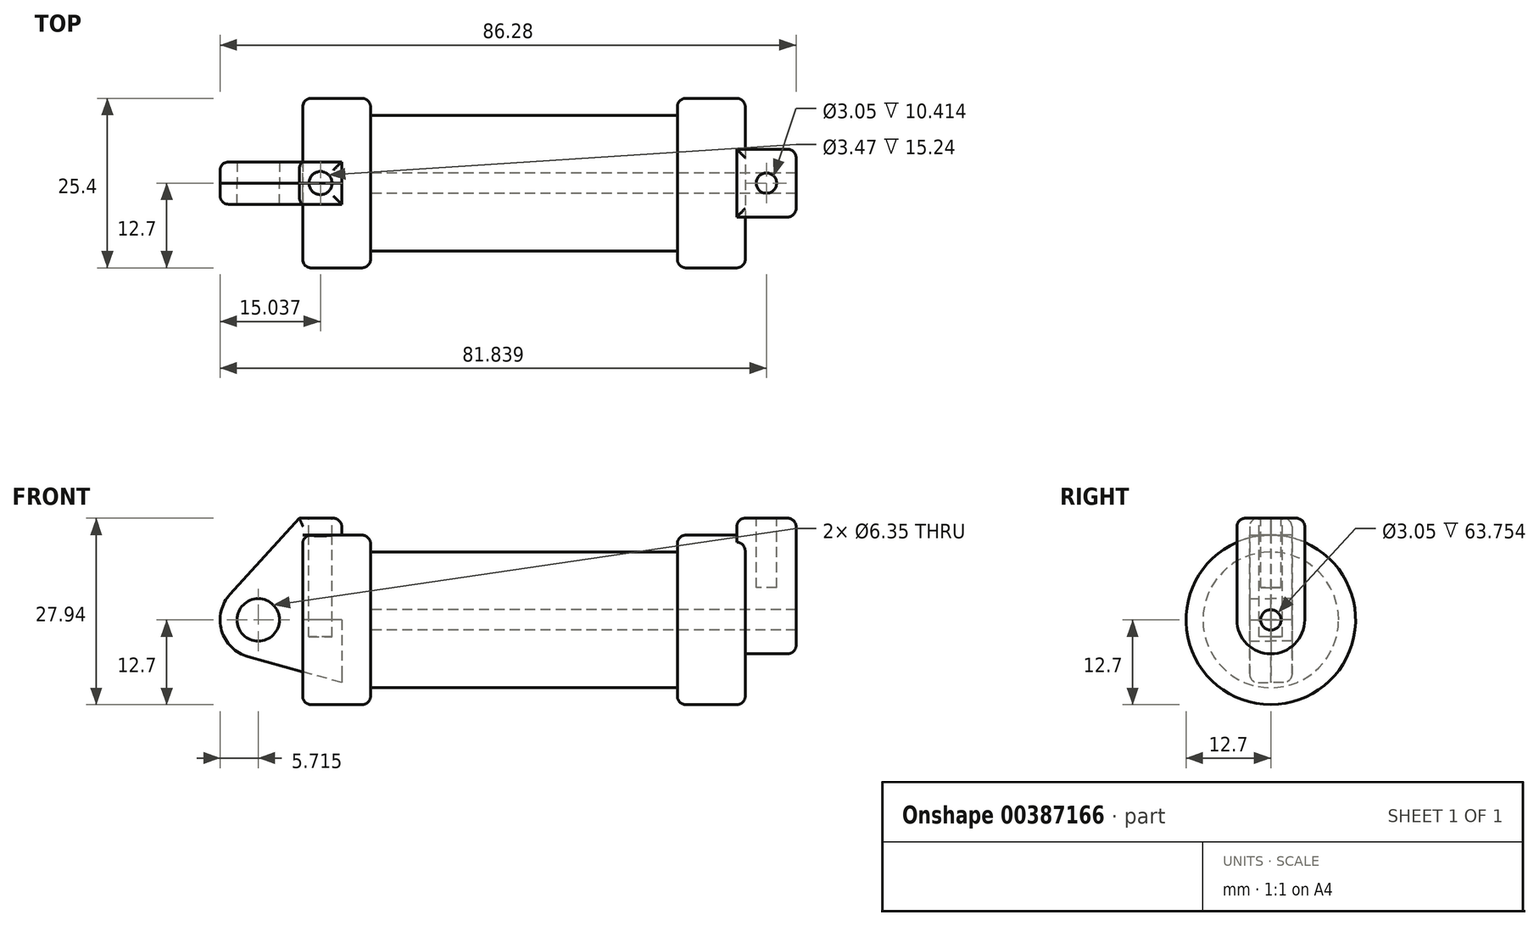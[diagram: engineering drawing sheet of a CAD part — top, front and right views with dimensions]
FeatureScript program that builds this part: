
annotation { "Feature Type Name" : "Feature", "Feature Type Description" : "" }
export const myFeature = defineFeature(function(context is Context, id is Id, definition is map)
    precondition{}
    {
        {
            var Q0;
            Q0=qCreatedBy(makeId("Front.planeOp"),FACE);
            var sketch = newSketch(context, id + "F0", { "sketchPlane" : qUnion([Q0])});
            skLineSegment(sketch, "E0", {"start": v(0, 0) * mm, "end": v(0, 12.7) * mm});
            skLineSegment(sketch, "E1", {"start": v(0, 12.7) * mm, "end": v(10.16, 12.7) * mm});
            skLineSegment(sketch, "E2", {"start": v(10.16, 12.7) * mm, "end": v(10.16, 10.16) * mm});
            skLineSegment(sketch, "E3", {"start": v(10.16, 10.16) * mm, "end": v(56.13, 10.16) * mm});
            skLineSegment(sketch, "E4", {"start": v(56.13, 10.16) * mm, "end": v(56.13, 12.7) * mm});
            skLineSegment(sketch, "E5", {"start": v(56.13, 12.7) * mm, "end": v(66.3, 12.7) * mm});
            skLineSegment(sketch, "E6", {"start": v(66.3, 12.7) * mm, "end": v(66.3, 0) * mm});
            skLineSegment(sketch, "E7", {"start": v(66.3, 0) * mm, "end": v(0, 0) * mm});
            skLineSegment(sketch, "E8", {"start": v(5.84, 15.24) * mm, "end": v(-0.5, 15.24) * mm});
            skLineSegment(sketch, "E9", {"start": v(-0.5, 15.24) * mm, "end": v(-10.88, 3.85) * mm});
            skLineSegment(sketch, "E10", {"start": v(0, 0) * mm, "end": v(-6.65, 0) * mm});
            skCircle(sketch, "E11", {"center": v(-6.65, 0) * mm, "radius": 5.72 * mm});
            skCircle(sketch, "E12", {"center": v(-6.65, 0) * mm, "radius": 3.18 * mm});
            skLineSegment(sketch, "E13", {"start": v(5.84, 15.24) * mm, "end": v(5.84, -9.4) * mm});
            skLineSegment(sketch, "E14", {"start": v(5.84, -9.4) * mm, "end": v(-8.18, -5.5) * mm});
            skSolve(sketch);
        }
        {
            var Q0;
            {var subQ0=sQuery(id+"F0.wireOp",EDGE,"E0");Q0=makeQuery(id+"F0.imprint","IMPRINT",FACE,{"disambiguationData":[TD([[makeQuery(id+"F0.imprint","IMPRINT",EDGE,{"derivedFrom":subQ0}),-1.0]])]});}
            var Q1;
            Q1=sQuery(id+"F0.wireOp",EDGE,"E7");
            revolve(context, id + "F1", {"entities" : qUnion([Q0]), "axis" : qUnion([Q1]), "revolveType" : RevolveType.FULL});
        }
        {
            var Q0;
            {var subQ0=sQuery(id+"F0.wireOp",EDGE,"E2");Q0=makeQuery(id+"F0.imprint","IMPRINT",FACE,{"disambiguationData":[TD([[makeQuery(id+"F0.imprint","IMPRINT",EDGE,{"derivedFrom":subQ0}),-1.0]])]});}
            var Q1;
            Q1=sQuery(id+"F0.wireOp",EDGE,"E7");
            revolve(context, id + "F2", {"operationType" : NewBodyOperationType.ADD, "entities" : qUnion([Q0]), "axis" : qUnion([Q1]), "revolveType" : RevolveType.FULL});
        }
        {
            var Q0;
            {var subQ5=sQuery(id+"F0.wireOp",EDGE,"E12");Q0=makeQuery(id+"F0.imprint","IMPRINT",FACE,{"disambiguationData":[TD([[makeQuery(id+"F0.imprint","IMPRINT",EDGE,{"derivedFrom":subQ5}),-1.0]])]});}
            var Q1;
            {var subQ0=sQuery(id+"F0.wireOp",EDGE,"E14");Q1=makeQuery(id+"F0.imprint","IMPRINT",FACE,{"disambiguationData":[TD([[makeQuery(id+"F0.imprint","IMPRINT",EDGE,{"derivedFrom":subQ0}),-1.0]])]});}
            var Q2;
            {var subQ1=sQuery(id+"F0.wireOp",EDGE,"E0");Q2=makeQuery(id+"F0.imprint","IMPRINT",FACE,{"disambiguationData":[TD([[makeQuery(id+"F0.imprint","IMPRINT",EDGE,{"derivedFrom":subQ1}),1.0]])]});}
            extrude(context, id + "F3", {"entities" : qUnion([Q0, Q1, Q2]), "depth" : 3.17 * mm});
        }
        {
            var Q0;
            {var subQ1=sQuery(id+"F0.wireOp",EDGE,"E0");Q0=makeQuery(id+"F0.imprint","IMPRINT",FACE,{"disambiguationData":[TD([[makeQuery(id+"F0.imprint","IMPRINT",EDGE,{"derivedFrom":subQ1}),1.0]])]});}
            var Q1;
            {var subQ5=sQuery(id+"F0.wireOp",EDGE,"E12");Q1=makeQuery(id+"F0.imprint","IMPRINT",FACE,{"disambiguationData":[TD([[makeQuery(id+"F0.imprint","IMPRINT",EDGE,{"derivedFrom":subQ5}),-1.0]])]});}
            var Q2;
            {var subQ0=sQuery(id+"F0.wireOp",EDGE,"E14");Q2=makeQuery(id+"F0.imprint","IMPRINT",FACE,{"disambiguationData":[TD([[makeQuery(id+"F0.imprint","IMPRINT",EDGE,{"derivedFrom":subQ0}),-1.0]])]});}
            extrude(context, id + "F4", {"entities" : qUnion([Q0, Q1, Q2]), "oppositeDirection" : true, "depth" : 3.17 * mm});
        }
        {
            var Q0;
            Q0=makeQuery(id+"F2.opRevolve","SWEPT_FACE",FACE,{"disambiguationData":[OSD([sQuery(id+"F0.wireOp",EDGE,"E6")])]});
            var sketch = newSketch(context, id + "F5", { "sketchPlane" : qUnion([Q0])});
            skCircle(sketch, "E15", {"center": v(0, 0) * mm, "radius": 1.52 * mm});
            skCircle(sketch, "E16", {"center": v(0, 0) * mm, "radius": 5.08 * mm});
            skLineSegment(sketch, "E17", {"start": v(-5.08, 0) * mm, "end": v(-5.08, 15.24) * mm});
            skLineSegment(sketch, "E18", {"start": v(5.08, 0) * mm, "end": v(5.08, 15.24) * mm});
            skLineSegment(sketch, "E19", {"start": v(-5.08, 15.24) * mm, "end": v(-3.2, 15.24) * mm});
            skLineSegment(sketch, "E20", {"start": v(-3.2, 15.24) * mm, "end": v(5.08, 15.24) * mm});
            skSolve(sketch);
        }
        {
            var Q0;
            Q0 = qSketchRegion(id + "F5", true);
            extrude(context, id + "F6", {"entities" : qUnion([Q0]), "operationType" : NewBodyOperationType.ADD, "depth" : 7.62 * mm});
        }
        {
            var Q0;
            Q0 = qSketchRegion(id + "F5", true);
            var Q1;
            Q1=makeQuery(id+"F5.imprint","IMPRINT",FACE,{"disambiguationData":[TD([[makeQuery(id+"F5.imprint","IMPRINT",EDGE,{"derivedFrom":sQuery(id+"F5.wireOp",EDGE,"E15")}),1.0]])]});
            extrude(context, id + "F7", {"entities" : qUnion([Q0, Q1]), "operationType" : NewBodyOperationType.ADD, "oppositeDirection" : true, "depth" : 1.27 * mm});
        }
        {
            var Q0;
            Q0=makeQuery(id+"F6.boolean.opBoolean","SPLIT",FACE,{"disambiguationData":[TD([makeQuery(id+"F6.opExtrude","SWEPT_FACE",FACE,{"disambiguationData":[OSD([sQuery(id+"F5.wireOp",EDGE,"E15")])]})])],"derivedFrom":makeQuery(id+"F2.opRevolve","SWEPT_FACE",FACE,{"disambiguationData":[OSD([sQuery(id+"F0.wireOp",EDGE,"E6")])]})});
            var Q1;
            Q1=makeQuery(id+"F2.opRevolve","SWEPT_FACE",FACE,{"disambiguationData":[OSD([sQuery(id+"F0.wireOp",EDGE,"E2")])]});
            extrude(context, id + "F8", {"entities" : qUnion([Q0]), "operationType" : NewBodyOperationType.REMOVE, "endBound" : BoundingType.UP_TO_SURFACE, "oppositeDirection" : true, "endBoundEntityFace" : qUnion([Q1]), "depth" : 25.4 * mm});
        }
        {
            var Q0;
            {var subQ0=sQuery(id+"F5.wireOp",EDGE,"E20");var subQ1=sQuery(id+"F5.wireOp",EDGE,"E19");Q0=makeQuery(id+"F7.boolean.opBoolean","MERGE",FACE,{"derivedFrom":[makeQuery(id+"F6.opExtrude","SWEPT_FACE",FACE,{"disambiguationData":[OSD([subQ1,subQ0])]}),makeQuery(id+"F7.opExtrude","SWEPT_FACE",FACE,{"disambiguationData":[OSD([subQ1,subQ0])]})]});}
            var sketch = newSketch(context, id + "F9", { "sketchPlane" : qUnion([Q0])});
            skLineSegment(sketch, "E21", {"start": v(69.47, 5.08) * mm, "end": v(69.47, -5.08) * mm, "construction": true});
            skLineSegment(sketch, "E22", {"start": v(73.91, 0) * mm, "end": v(65.02, 0) * mm, "construction": true});
            skCircle(sketch, "E23", {"center": v(69.47, 0) * mm, "radius": 1.52 * mm});
            skSolve(sketch);
        }
        {
            var Q0;
            Q0=makeQuery(id+"F9.imprint","IMPRINT",FACE,{"disambiguationData":[TD([[makeQuery(id+"F9.imprint","IMPRINT",EDGE,{"derivedFrom":sQuery(id+"F9.wireOp",EDGE,"E23")}),1.0]])]});
            extrude(context, id + "F10", {"entities" : qUnion([Q0]), "operationType" : NewBodyOperationType.REMOVE, "oppositeDirection" : true, "depth" : 10.4 * mm});
        }
        {
            var Q0;
            Q0=makeQuery(id+"F4.opExtrude","SWEPT_FACE",FACE,{"disambiguationData":[OSD([sQuery(id+"F0.wireOp",EDGE,"E8")])]});
            var sketch = newSketch(context, id + "F11", { "sketchPlane" : qUnion([Q0])});
            skCircle(sketch, "E24", {"center": v(2.67, 0) * mm, "radius": 1.73 * mm});
            skSolve(sketch);
        }
        {
            var Q0;
            {var subQ0=sQuery(id+"F11.wireOp",EDGE,"E24");var subQ1=makeQuery(id+"F4.opExtrude","CAP_EDGE",EDGE,{"disambiguationData":[OSD([sQuery(id+"F0.wireOp",EDGE,"E8")])],"isStart":true});var subQ2=makeQuery(id+"F11.imprint","INTERSECT",VERTEX,{"disambiguationData":[OD(0.0)],"derivedFrom":[subQ1,subQ0]});Q0=makeQuery(id+"F11.imprint","IMPRINT",FACE,{"disambiguationData":[TD([[makeQuery(id+"F11.imprint","IMPRINT",EDGE,{"disambiguationData":[TD([[subQ2,-1.0]])],"derivedFrom":subQ0}),1.0]])]});}
            var Q1;
            {var subQ0=sQuery(id+"F11.wireOp",EDGE,"E24");var subQ1=makeQuery(id+"F4.opExtrude","CAP_EDGE",EDGE,{"disambiguationData":[OSD([sQuery(id+"F0.wireOp",EDGE,"E8")])],"isStart":true});var subQ2=makeQuery(id+"F11.imprint","INTERSECT",VERTEX,{"disambiguationData":[OD(0.0)],"derivedFrom":[subQ1,subQ0]});Q1=makeQuery(id+"F11.imprint","IMPRINT",FACE,{"disambiguationData":[TD([[makeQuery(id+"F11.imprint","IMPRINT",EDGE,{"disambiguationData":[TD([[subQ2,1.0]])],"derivedFrom":subQ0}),1.0]])]});}
            extrude(context, id + "F12", {"entities" : qUnion([Q0, Q1]), "operationType" : NewBodyOperationType.REMOVE, "oppositeDirection" : true, "depth" : 17.78 * mm});
        }
        {
            var Q0;
            {var subQ0=sQuery(id+"F11.wireOp",EDGE,"E24");var subQ1=makeQuery(id+"F4.opExtrude","CAP_EDGE",EDGE,{"disambiguationData":[OSD([sQuery(id+"F0.wireOp",EDGE,"E8")])],"isStart":true});var subQ2=makeQuery(id+"F11.imprint","INTERSECT",VERTEX,{"disambiguationData":[OD(0.0)],"derivedFrom":[subQ1,subQ0]});Q0=makeQuery(id+"F11.imprint","IMPRINT",FACE,{"disambiguationData":[TD([[makeQuery(id+"F11.imprint","IMPRINT",EDGE,{"disambiguationData":[TD([[subQ2,1.0]])],"derivedFrom":subQ0}),1.0]])]});}
            extrude(context, id + "F13", {"entities" : qUnion([Q0]), "operationType" : NewBodyOperationType.REMOVE, "oppositeDirection" : true, "depth" : 17.78 * mm});
        }
        {
            var Q0;
            Q0=makeQuery(id+"F2.opRevolve","SWEPT_EDGE",EDGE,{"disambiguationData":[OSD([sQuery(id+"F0.wireOp",EDGE,"E1"),sQuery(id+"F0.wireOp",EDGE,"E2")])]});
            fillet(context, id + "F14", {"entities" : qUnion([Q0]), "radius" : 1.27 * mm, "tangentPropagation" : true, "allowEdgeOverflow" : false});
        }
        {
            var Q0;
            {var subQ0=sQuery(id+"F0.wireOp",EDGE,"E5");var subQ1=sQuery(id+"F0.wireOp",EDGE,"E6");Q0=makeQuery(id+"F6.boolean.opBoolean","SPLIT",EDGE,{"disambiguationData":[topologyDisambiguationEdgeConnected([makeQuery(id+"F2.opRevolve","SWEPT_FACE",FACE,{"disambiguationData":[OSD([subQ1])]})])],"derivedFrom":makeQuery(id+"F2.opRevolve","SWEPT_EDGE",EDGE,{"disambiguationData":[OSD([subQ0,subQ1])]})});}
            var Q1;
            Q1=makeQuery(id+"F6.opExtrude","CAP_EDGE",EDGE,{"disambiguationData":[OSD([sQuery(id+"F5.wireOp",EDGE,"E19"),sQuery(id+"F5.wireOp",EDGE,"E20")])],"isStart":false});
            var Q2;
            Q2=makeQuery(id+"F3.opExtrude","CAP_EDGE",EDGE,{"disambiguationData":[OSD([sQuery(id+"F0.wireOp",EDGE,"E8")])],"isStart":false});
            var Q3;
            Q3=makeQuery(id+"F4.opExtrude","CAP_EDGE",EDGE,{"disambiguationData":[OSD([sQuery(id+"F0.wireOp",EDGE,"E8")])],"isStart":false});
            var Q4;
            Q4=makeQuery(id+"F4.opExtrude","SWEPT_EDGE",EDGE,{"disambiguationData":[OSD([sQuery(id+"F0.wireOp",EDGE,"E8"),sQuery(id+"F0.wireOp",EDGE,"E13")])]});
            var Q5;
            Q5=makeQuery(id+"F2.opRevolve","SWEPT_EDGE",EDGE,{"disambiguationData":[OSD([sQuery(id+"F0.wireOp",EDGE,"E4"),sQuery(id+"F0.wireOp",EDGE,"E5")])]});
            var Q6;
            Q6=makeQuery(id+"F3.opExtrude","SWEPT_EDGE",EDGE,{"disambiguationData":[OSD([sQuery(id+"F0.wireOp",EDGE,"E8"),sQuery(id+"F0.wireOp",EDGE,"E13")])]});
            var Q7;
            Q7=makeQuery(id+"F1.opRevolve","SWEPT_EDGE",EDGE,{"disambiguationData":[OSD([sQuery(id+"F0.wireOp",EDGE,"E0"),sQuery(id+"F0.wireOp",EDGE,"E1")])]});
            var Q8;
            {var subQ0=sQuery(id+"F5.wireOp",EDGE,"E19");var subQ1=sQuery(id+"F5.wireOp",EDGE,"E17");Q8=makeQuery(id+"F7.boolean.opBoolean","MERGE",EDGE,{"derivedFrom":[makeQuery(id+"F6.opExtrude","SWEPT_EDGE",EDGE,{"disambiguationData":[OSD([subQ1,subQ0])]}),makeQuery(id+"F7.opExtrude","SWEPT_EDGE",EDGE,{"disambiguationData":[OSD([subQ1,subQ0])]})]});}
            var Q9;
            Q9=makeQuery(id+"F7.opExtrude","CAP_EDGE",EDGE,{"disambiguationData":[OSD([sQuery(id+"F5.wireOp",EDGE,"E19"),sQuery(id+"F5.wireOp",EDGE,"E20")])],"isStart":false});
            var Q10;
            {var subQ0=sQuery(id+"F5.wireOp",EDGE,"E20");var subQ1=sQuery(id+"F5.wireOp",EDGE,"E18");Q10=makeQuery(id+"F7.boolean.opBoolean","MERGE",EDGE,{"derivedFrom":[makeQuery(id+"F6.opExtrude","SWEPT_EDGE",EDGE,{"disambiguationData":[OSD([subQ1,subQ0])]}),makeQuery(id+"F7.opExtrude","SWEPT_EDGE",EDGE,{"disambiguationData":[OSD([subQ1,subQ0])]})]});}
            var Q11;
            Q11=makeQuery(id+"F4.opExtrude","CAP_EDGE",EDGE,{"disambiguationData":[OSD([sQuery(id+"F0.wireOp",EDGE,"E9")])],"isStart":false});
            var Q12;
            Q12=makeQuery(id+"F3.opExtrude","CAP_EDGE",EDGE,{"disambiguationData":[OSD([sQuery(id+"F0.wireOp",EDGE,"E11")])],"isStart":false});
            var Q13;
            Q13=makeQuery(id+"F6.opExtrude","CAP_EDGE",EDGE,{"disambiguationData":[OSD([sQuery(id+"F5.wireOp",EDGE,"E17")])],"isStart":false});
            fillet(context, id + "F15", {"entities" : qUnion([Q0, Q1, Q2, Q3, Q4, Q5, Q6, Q7, Q8, Q9, Q10, Q11, Q12, Q13]), "radius" : 1.27 * mm, "tangentPropagation" : true, "allowEdgeOverflow" : false});
        }
    });
